# Revit family: ST1030001 Plumbing-Fix_Faucet-Touchless_Stern_Dolphin
name_source: partatom
category: Aparatos sanitarios
revit_build: Autodesk Revit 2018 (Build: 20170223_1515(x64)
units: mm (PartAtom-declared; Revit-internal decimal feet)

## family parameters
Anfitrión = Cara
Compartido = No
Corte con vacíos al cargar = No
Cota de conector redondo = Diámetro de uso
Número OmniClass = 23.45.55.14
Punto de cálculo de habitación = No
Tipo de pieza = Normal
Título OmniClass = Single Faucets

## types (1)
- Battery Pack 1.58 GPM
    Accionamiento = Sensor
    Available Options = as Specified
    CWFU = 1
    Comentarios de tipo = as Specified
    Conexión AC = Sí
    Conexión AF = Sí
    Conexión de residuos = No
    Conexión de ventilación = No
    Costo = 0 $
    Cumple EDGE = Sí
    Cumple LEED = Sí
    Código de montaje = D2010300
    Descripción = Stern Touchless Deck Mounted Faucet - Dolphin FB as Specified
    Diámetro de conexión = 1/2 pulg. NPSM / de la manguera
    Elevación por defecto = 0 mm
    Expected Lifespan (Years) = 0
    Fabricante = Stern Engineering
    Garantía = Garantía de 3 años por defectos de fabricación y cromados. 1 año de garantía para el sistema electrónico.
    HWFU = 1
    Maintenance Schedule (Months) = 0
    Marca = CORONA
    Material de Fabricación = Latón y componentes poliméricos
    Modelo = Dolphin FB
    Nombre = Grifería Lavamanos Dolphin Sensor
    Nota clave = 22 40 00
    Operating Pressure Range = 7.26 - 116 PSI  ;  0.5 - 8 bar
    Operating Temperature Range = Up to 149 F / 65 C
    Piping_Flow = 0 GPM
    Piping_Inlet Diameter = 1"
    Power Supply = 9V Battery
    Presión Máxima = 80 Psi
    Presión Mínima = 20 Psi
    Product Features = Security Shut Off Timer
    Referencia = ST1030001
    Revision = R1_2018-04
    Spout Height = 178 mm
    Spout Reach = 0 mm
    Standards Conformance = as Specified
    Tipo = Grifería Lavamanos
    Tráfico = Institucional, alto tráfico
    URL = https://www.corona.co
    Unit Height = 0 mm
    Unit Width = 51 mm
    Vida útil ( ciclos ) = 150.000
    WFU = 0
    Warranty Duration (Years) = 2

## geometry (parser evidence)
native form markers: Sweep x2
no freeform markers — native parametric forms only
